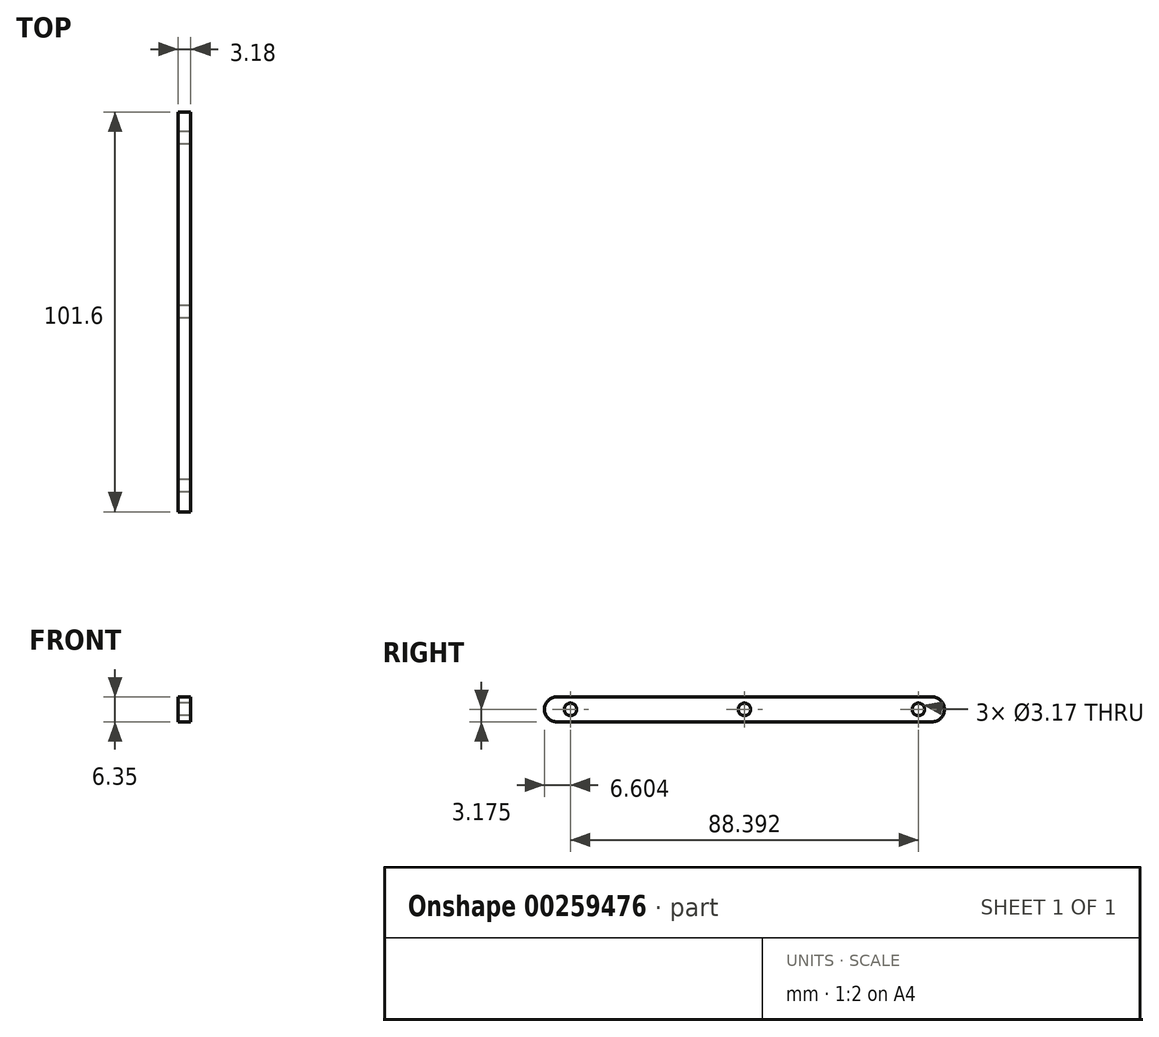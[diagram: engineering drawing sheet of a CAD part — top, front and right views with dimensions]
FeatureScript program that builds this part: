
annotation { "Feature Type Name" : "Feature", "Feature Type Description" : "" }
export const myFeature = defineFeature(function(context is Context, id is Id, definition is map)
    precondition{}
    {
        {
            var Q0;
            Q0=qCreatedBy(makeId("Right.planeOp"),FACE);
            var sketch = newSketch(context, id + "F0", { "sketchPlane" : qUnion([Q0])});
            skLineSegment(sketch, "E0.bottom", {"start": v(0, 0) * mm, "end": v(101.6, 0) * mm});
            skLineSegment(sketch, "E0.top", {"start": v(0, -6.35) * mm, "end": v(101.6, -6.35) * mm});
            skLineSegment(sketch, "E0.left", {"start": v(0, 0) * mm, "end": v(0, -6.35) * mm});
            skLineSegment(sketch, "E0.right", {"start": v(101.6, 0) * mm, "end": v(101.6, -6.35) * mm});
            skCircle(sketch, "E1", {"center": v(6.6, -3.18) * mm, "radius": 1.59 * mm});
            skCircle(sketch, "E2", {"center": v(50.8, -3.18) * mm, "radius": 1.59 * mm});
            skCircle(sketch, "E3", {"center": v(95, -3.18) * mm, "radius": 1.59 * mm});
            skSolve(sketch);
        }
        {
            var Q0;
            Q0=makeQuery(id+"F0.imprint","IMPRINT",FACE,{"disambiguationData":[TD([[makeQuery(id+"F0.imprint","IMPRINT",EDGE,{"derivedFrom":sQuery(id+"F0.wireOp",EDGE,"E0.bottom")}),-1.0]])]});
            extrude(context, id + "F1", {"entities" : qUnion([Q0]), "depth" : 3.17 * mm});
        }
        {
            var Q0;
            Q0=makeQuery(id+"F1.opExtrude","SWEPT_EDGE",EDGE,{"disambiguationData":[OSD([sQuery(id+"F0.wireOp",EDGE,"E0.bottom"),sQuery(id+"F0.wireOp",EDGE,"E0.left")])]});
            var Q1;
            Q1=makeQuery(id+"F1.opExtrude","SWEPT_EDGE",EDGE,{"disambiguationData":[OSD([sQuery(id+"F0.wireOp",EDGE,"E0.top"),sQuery(id+"F0.wireOp",EDGE,"E0.left")])]});
            fillet(context, id + "F2", {"entities" : qUnion([Q0, Q1]), "radius" : 3.17 * mm, "tangentPropagation" : true, "allowEdgeOverflow" : false});
        }
        {
            var Q0;
            Q0=makeQuery(id+"F1.opExtrude","SWEPT_EDGE",EDGE,{"disambiguationData":[OSD([sQuery(id+"F0.wireOp",EDGE,"E0.bottom"),sQuery(id+"F0.wireOp",EDGE,"E0.right")])]});
            var Q1;
            Q1=makeQuery(id+"F1.opExtrude","SWEPT_EDGE",EDGE,{"disambiguationData":[OSD([sQuery(id+"F0.wireOp",EDGE,"E0.top"),sQuery(id+"F0.wireOp",EDGE,"E0.right")])]});
            fillet(context, id + "F3", {"entities" : qUnion([Q0, Q1]), "radius" : 3.17 * mm, "tangentPropagation" : true, "allowEdgeOverflow" : false});
        }
    });
